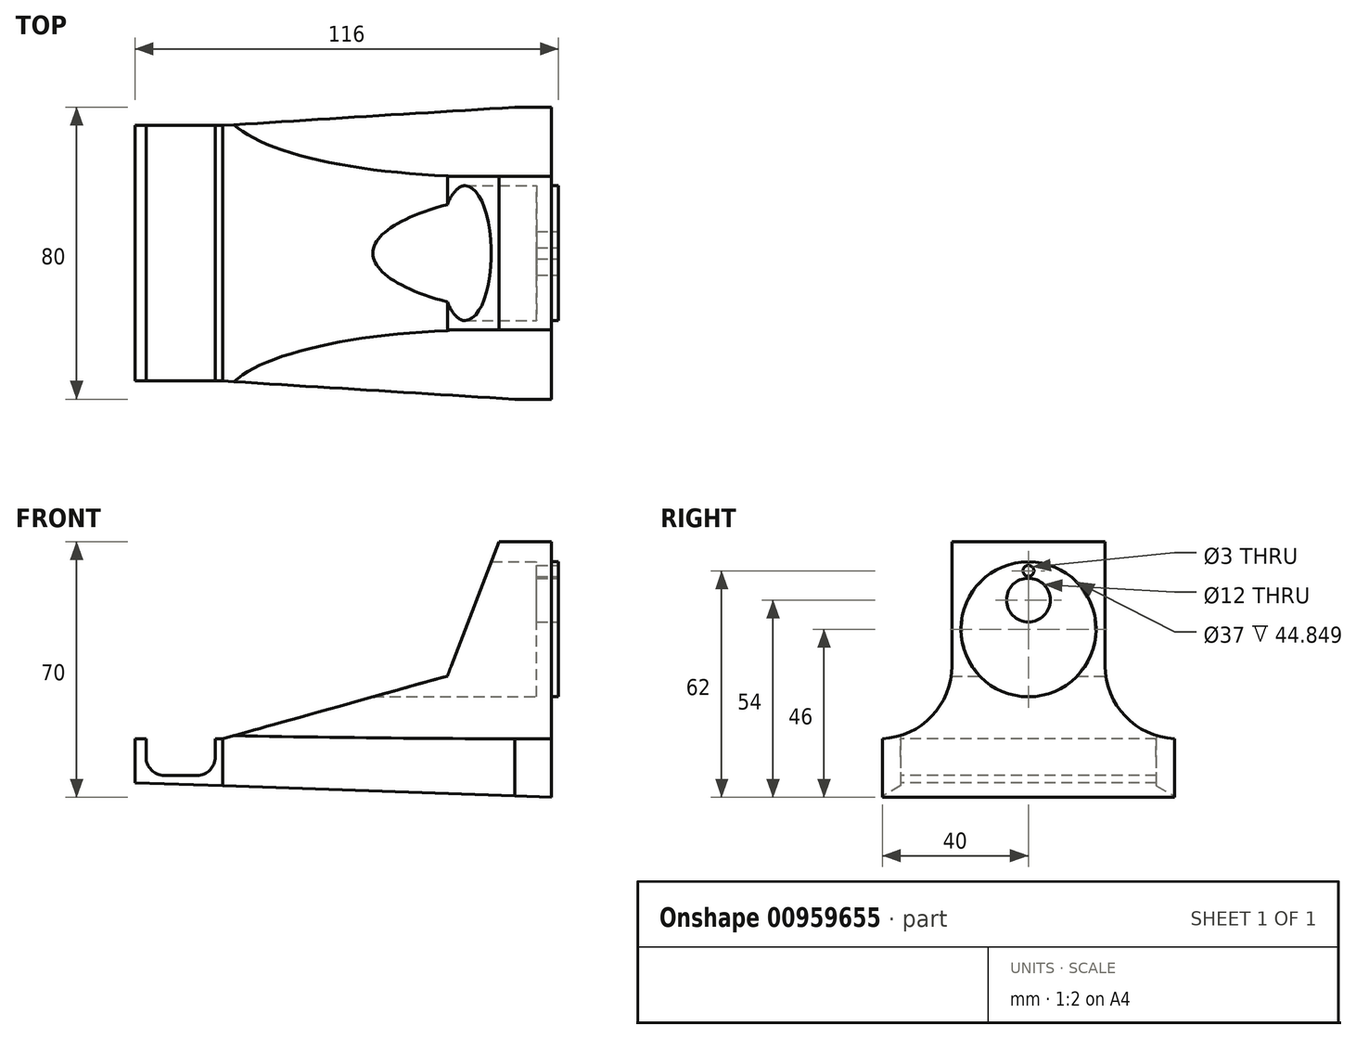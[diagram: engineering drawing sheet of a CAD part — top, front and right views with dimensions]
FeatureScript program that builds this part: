
annotation { "Feature Type Name" : "Feature", "Feature Type Description" : "" }
export const myFeature = defineFeature(function(context is Context, id is Id, definition is map)
    precondition{}
    {
        {
            var Q0;
            Q0=qCreatedBy(makeId("Right.planeOp"),FACE);
            var sketch = newSketch(context, id + "F0", { "sketchPlane" : qUnion([Q0])});
            skCircle(sketch, "E0", {"center": v(0, 0) * mm, "radius": 18.5 * mm});
            skSolve(sketch);
        }
        {
            var Q0;
            Q0=makeQuery(id+"F0.imprint","IMPRINT",FACE,{"disambiguationData":[TD([[makeQuery(id+"F0.imprint","IMPRINT",EDGE,{"derivedFrom":sQuery(id+"F0.wireOp",EDGE,"E0")}),1.0]])]});
            extrude(context, id + "F1", {"entities" : qUnion([Q0]), "depth" : 2 * mm, "offsetDistance" : 25 * mm});
        }
        {
            var Q0;
            Q0=makeQuery(id+"F1.opExtrude","CAP_FACE",FACE,{"disambiguationData":[OSD([sQuery(id+"F0.wireOp",EDGE,"E0")])],"isStart":false});
            var sketch = newSketch(context, id + "F2", { "sketchPlane" : qUnion([Q0])});
            skCircle(sketch, "E1", {"center": v(0, 16) * mm, "radius": 1.5 * mm});
            skSolve(sketch);
        }
        {
            var Q0;
            Q0=makeQuery(id+"F2.imprint","IMPRINT",FACE,{"disambiguationData":[TD([[makeQuery(id+"F2.imprint","IMPRINT",EDGE,{"derivedFrom":sQuery(id+"F2.wireOp",EDGE,"E1")}),1.0]])]});
            extrude(context, id + "F3", {"entities" : qUnion([Q0]), "operationType" : NewBodyOperationType.REMOVE, "oppositeDirection" : true, "depth" : 25 * mm, "offsetDistance" : 25 * mm});
        }
        {
            var Q0;
            Q0=qCreatedBy(makeId("Top.planeOp"),FACE);
            var sketch = newSketch(context, id + "F4", { "sketchPlane" : qUnion([Q0])});
            skLineSegment(sketch, "E2", {"start": v(0, 0) * mm, "end": v(32.12, 0) * mm, "construction": true});
            skSolve(sketch);
        }
        {
            var Q0;
            Q0=makeQuery(id+"F1.opExtrude","CAP_FACE",FACE,{"disambiguationData":[OSD([sQuery(id+"F0.wireOp",EDGE,"E0")])],"isStart":false});
            var sketch = newSketch(context, id + "F5", { "sketchPlane" : qUnion([Q0])});
            skCircle(sketch, "E3", {"center": v(0, 8) * mm, "radius": 6 * mm});
            skSolve(sketch);
        }
        {
            var Q0;
            Q0=makeQuery(id+"F5.imprint","IMPRINT",FACE,{"disambiguationData":[TD([[makeQuery(id+"F5.imprint","IMPRINT",EDGE,{"derivedFrom":sQuery(id+"F5.wireOp",EDGE,"E3")}),1.0]])]});
            extrude(context, id + "F6", {"entities" : qUnion([Q0]), "operationType" : NewBodyOperationType.REMOVE, "oppositeDirection" : true, "depth" : 25 * mm, "offsetDistance" : 25 * mm});
        }
        {
            var Q0;
            Q0=qCreatedBy(makeId("Right.planeOp"),FACE);
            var sketch = newSketch(context, id + "F7", { "sketchPlane" : qUnion([Q0])});
            skLineSegment(sketch, "E4.bottom", {"start": v(-21, -46) * mm, "end": v(21, -46) * mm});
            skLineSegment(sketch, "E4.top", {"start": v(-21, 24) * mm, "end": v(21, 24) * mm});
            skLineSegment(sketch, "E4.left", {"start": v(-21, -46) * mm, "end": v(-21, 24) * mm});
            skLineSegment(sketch, "E4.right", {"start": v(21, -46) * mm, "end": v(21, 24) * mm});
            skPoint(sketch, "E4.middle", {"position": v(0, -11) * mm});
            skLineSegment(sketch, "E5.bottom", {"start": v(-40, -46) * mm, "end": v(40, -46) * mm});
            skLineSegment(sketch, "E5.top", {"start": v(-40, -30) * mm, "end": v(40, -30) * mm});
            skLineSegment(sketch, "E5.left", {"start": v(-40, -46) * mm, "end": v(-40, -30) * mm});
            skLineSegment(sketch, "E5.right", {"start": v(40, -46) * mm, "end": v(40, -30) * mm});
            skPoint(sketch, "E5.middle", {"position": v(0, -38) * mm});
            skPoint(sketch, "E5.cornerSnap0", {"position": v(0, -46) * mm});
            skSolve(sketch);
        }
        {
            var Q0;
            {var subQ0=sQuery(id+"F7.wireOp",EDGE,"E4.top");Q0=makeQuery(id+"F7.imprint","IMPRINT",FACE,{"disambiguationData":[TD([[makeQuery(id+"F7.imprint","IMPRINT",EDGE,{"derivedFrom":subQ0}),-1.0]])]});}
            var Q1;
            {var subQ5=sQuery(id+"F7.wireOp",EDGE,"E5.right");Q1=makeQuery(id+"F7.imprint","IMPRINT",FACE,{"disambiguationData":[TD([[makeQuery(id+"F7.imprint","IMPRINT",EDGE,{"derivedFrom":subQ5}),1.0]])]});}
            var Q2;
            {var subQ0=sQuery(id+"F7.wireOp",EDGE,"E5.bottom");var subQ1=sQuery(id+"F7.wireOp",EDGE,"E4.left");var subQ2=makeQuery(id+"F7.imprint","INTERSECT",VERTEX,{"derivedFrom":[subQ1,subQ0]});Q2=makeQuery(id+"F7.imprint","IMPRINT",FACE,{"disambiguationData":[TD([[makeQuery(id+"F7.imprint","IMPRINT",EDGE,{"disambiguationData":[TD([[subQ2,-1.0]])],"derivedFrom":subQ1}),-1.0]])]});}
            var Q3;
            {var subQ5=sQuery(id+"F7.wireOp",EDGE,"E5.left");Q3=makeQuery(id+"F7.imprint","IMPRINT",FACE,{"disambiguationData":[TD([[makeQuery(id+"F7.imprint","IMPRINT",EDGE,{"derivedFrom":subQ5}),-1.0]])]});}
            extrude(context, id + "F8", {"entities" : qUnion([Q0, Q1, Q2, Q3]), "operationType" : NewBodyOperationType.ADD, "oppositeDirection" : true, "depth" : 90 * mm, "offsetDistance" : 25 * mm});
        }
        {
            var Q0;
            Q0=qCreatedBy(makeId("Right.planeOp"),FACE);
            cPlane(context, id + "F9", {"entities" : qUnion([Q0]), "cplaneType" : CPlaneType.OFFSET, "offset" : 4 * mm, "oppositeDirection" : true, "width" : 150 * mm, "height" : 150 * mm});
        }
        {
            var Q0;
            Q0=qCreatedBy(id+"F9.planeOp",FACE);
            var sketch = newSketch(context, id + "F10", { "sketchPlane" : qUnion([Q0])});
            skCircle(sketch, "E6", {"center": v(0, 0) * mm, "radius": 18.5 * mm});
            skSolve(sketch);
        }
        {
            var Q0;
            Q0 = qSketchRegion(id + "F10", true);
            var Q1;
            Q1=makeQuery(id+"F8.boolean.opBoolean","SPLIT",FACE,{"disambiguationData":[TD([makeQuery(id+"F6.boolean.opBoolean","COPY",FACE,{"derivedFrom":makeQuery(id+"F6.opExtrude","SWEPT_FACE",FACE,{"disambiguationData":[OSD([sQuery(id+"F5.wireOp",EDGE,"E3")])]})})])],"derivedFrom":makeQuery(id+"F8.opExtrude","CAP_FACE",FACE,{"disambiguationData":[OSD([sQuery(id+"F7.wireOp",EDGE,"E4.top"),sQuery(id+"F7.wireOp",EDGE,"E4.left"),sQuery(id+"F7.wireOp",EDGE,"E4.right"),sQuery(id+"F7.wireOp",EDGE,"E5.bottom"),sQuery(id+"F7.wireOp",EDGE,"E5.top"),sQuery(id+"F7.wireOp",EDGE,"E5.left"),sQuery(id+"F7.wireOp",EDGE,"E5.right")])],"isStart":true})});
            extrude(context, id + "F11", {"entities" : qUnion([Q0, Q1]), "operationType" : NewBodyOperationType.REMOVE, "oppositeDirection" : true, "depth" : 80 * mm, "offsetDistance" : 25 * mm});
        }
        {
            var Q0;
            Q0=makeQuery(id+"F8.opExtrude","SWEPT_FACE",FACE,{"disambiguationData":[OSD([sQuery(id+"F7.wireOp",EDGE,"E4.right")])]});
            var sketch = newSketch(context, id + "F12", { "sketchPlane" : qUnion([Q0])});
            skLineSegment(sketch, "E7", {"start": v(14.3, 24) * mm, "end": v(28.45, -12.8) * mm});
            skLineSegment(sketch, "E8", {"start": v(28.45, -12.8) * mm, "end": v(90, -30) * mm});
            skLineSegment(sketch, "E9", {"start": v(90, -30) * mm, "end": v(90, 24) * mm});
            skLineSegment(sketch, "E10", {"start": v(90, 24) * mm, "end": v(14.3, 24) * mm});
            skSolve(sketch);
        }
        {
            var Q0;
            Q0=makeQuery(id+"F12.imprint","IMPRINT",FACE,{"disambiguationData":[TD([[makeQuery(id+"F12.imprint","IMPRINT",EDGE,{"derivedFrom":sQuery(id+"F12.wireOp",EDGE,"E7")}),1.0]])]});
            extrude(context, id + "F13", {"entities" : qUnion([Q0]), "operationType" : NewBodyOperationType.REMOVE, "endBound" : BoundingType.THROUGH_ALL, "oppositeDirection" : true, "depth" : 25 * mm, "offsetDistance" : 25 * mm});
        }
        {
            var Q0;
            Q0=makeQuery(id+"F8.boolean.opBoolean","SPLIT",FACE,{"disambiguationData":[TD([makeQuery(id+"F5O549hGg848MVX_1.1.F6.boolean.opBoolean","COPY",FACE,{"derivedFrom":makeQuery(id+"F5O549hGg848MVX_1.1.F6.opExtrude","SWEPT_FACE",FACE,{"disambiguationData":[OSD([sQuery(id+"F5.wireOp",EDGE,"E3")])]})})])],"derivedFrom":makeQuery(id+"F8.opExtrude","CAP_FACE",FACE,{"disambiguationData":[OSD([sQuery(id+"F7.wireOp",EDGE,"E4.top"),sQuery(id+"F7.wireOp",EDGE,"E4.left"),sQuery(id+"F7.wireOp",EDGE,"E4.right"),sQuery(id+"F7.wireOp",EDGE,"E5.bottom"),sQuery(id+"F7.wireOp",EDGE,"E5.top"),sQuery(id+"F7.wireOp",EDGE,"E5.left"),sQuery(id+"F7.wireOp",EDGE,"E5.right")])],"isStart":true})});
            var Q1;
            Q1=makeQuery(id+"F8.boolean.opBoolean","SPLIT",FACE,{"disambiguationData":[TD([makeQuery(id+"F3.boolean.opBoolean","COPY",FACE,{"derivedFrom":makeQuery(id+"F3.opExtrude","SWEPT_FACE",FACE,{"disambiguationData":[OSD([sQuery(id+"F2.wireOp",EDGE,"E1")])]})})])],"derivedFrom":makeQuery(id+"F8.opExtrude","CAP_FACE",FACE,{"disambiguationData":[OSD([sQuery(id+"F7.wireOp",EDGE,"E4.top"),sQuery(id+"F7.wireOp",EDGE,"E4.left"),sQuery(id+"F7.wireOp",EDGE,"E4.right"),sQuery(id+"F7.wireOp",EDGE,"E5.bottom"),sQuery(id+"F7.wireOp",EDGE,"E5.top"),sQuery(id+"F7.wireOp",EDGE,"E5.left"),sQuery(id+"F7.wireOp",EDGE,"E5.right")])],"isStart":true})});
            var Q2;
            Q2=makeQuery(id+"F8.boolean.opBoolean","SPLIT",FACE,{"disambiguationData":[TD([makeQuery(id+"F37mEyM0ohrxXI6_1.1.F3.boolean.opBoolean","COPY",FACE,{"derivedFrom":makeQuery(id+"F37mEyM0ohrxXI6_1.1.F3.opExtrude","SWEPT_FACE",FACE,{"disambiguationData":[OSD([sQuery(id+"F2.wireOp",EDGE,"E1")])]})})])],"derivedFrom":makeQuery(id+"F8.opExtrude","CAP_FACE",FACE,{"disambiguationData":[OSD([sQuery(id+"F7.wireOp",EDGE,"E4.top"),sQuery(id+"F7.wireOp",EDGE,"E4.left"),sQuery(id+"F7.wireOp",EDGE,"E4.right"),sQuery(id+"F7.wireOp",EDGE,"E5.bottom"),sQuery(id+"F7.wireOp",EDGE,"E5.top"),sQuery(id+"F7.wireOp",EDGE,"E5.left"),sQuery(id+"F7.wireOp",EDGE,"E5.right")])],"isStart":true})});
            var Q3;
            Q3=makeQuery(id+"F8.boolean.opBoolean","SPLIT",FACE,{"disambiguationData":[TD([makeQuery(id+"F37mEyM0ohrxXI6_1.2.F3.boolean.opBoolean","COPY",FACE,{"derivedFrom":makeQuery(id+"F37mEyM0ohrxXI6_1.2.F3.opExtrude","SWEPT_FACE",FACE,{"disambiguationData":[OSD([sQuery(id+"F2.wireOp",EDGE,"E1")])]})})])],"derivedFrom":makeQuery(id+"F8.opExtrude","CAP_FACE",FACE,{"disambiguationData":[OSD([sQuery(id+"F7.wireOp",EDGE,"E4.top"),sQuery(id+"F7.wireOp",EDGE,"E4.left"),sQuery(id+"F7.wireOp",EDGE,"E4.right"),sQuery(id+"F7.wireOp",EDGE,"E5.bottom"),sQuery(id+"F7.wireOp",EDGE,"E5.top"),sQuery(id+"F7.wireOp",EDGE,"E5.left"),sQuery(id+"F7.wireOp",EDGE,"E5.right")])],"isStart":true})});
            extrude(context, id + "F14", {"entities" : qUnion([Q0, Q1, Q2, Q3]), "operationType" : NewBodyOperationType.REMOVE, "oppositeDirection" : true, "depth" : 25 * mm, "offsetDistance" : 25 * mm});
        }
        {
            var Q0;
            Q0=makeQuery(id+"F8.opExtrude","CAP_FACE",FACE,{"disambiguationData":[OSD([sQuery(id+"F7.wireOp",EDGE,"E4.top"),sQuery(id+"F7.wireOp",EDGE,"E4.left"),sQuery(id+"F7.wireOp",EDGE,"E4.right"),sQuery(id+"F7.wireOp",EDGE,"E5.bottom"),sQuery(id+"F7.wireOp",EDGE,"E5.top"),sQuery(id+"F7.wireOp",EDGE,"E5.left"),sQuery(id+"F7.wireOp",EDGE,"E5.right")])],"isStart":false});
            var sketch = newSketch(context, id + "F15", { "sketchPlane" : qUnion([Q0])});
            skLineSegment(sketch, "E11.bottom", {"start": v(-35, -30) * mm, "end": v(35, -30) * mm});
            skLineSegment(sketch, "E11.top", {"start": v(-35, -46) * mm, "end": v(35, -46) * mm});
            skLineSegment(sketch, "E11.left", {"start": v(-35, -30) * mm, "end": v(-35, -46) * mm});
            skLineSegment(sketch, "E11.right", {"start": v(35, -30) * mm, "end": v(35, -46) * mm});
            skSolve(sketch);
        }
        {
            var Q0;
            Q0=makeQuery(id+"F15.imprint","IMPRINT",FACE,{"disambiguationData":[TD([[makeQuery(id+"F15.imprint","IMPRINT",EDGE,{"derivedFrom":sQuery(id+"F15.wireOp",EDGE,"E11.top")}),-1.0]])]});
            extrude(context, id + "F16", {"entities" : qUnion([Q0]), "operationType" : NewBodyOperationType.ADD, "depth" : 24 * mm, "offsetDistance" : 25 * mm});
        }
        {
            var Q0;
            Q0=makeQuery(id+"F16.opExtrude","SWEPT_FACE",FACE,{"disambiguationData":[OSD([sQuery(id+"F15.wireOp",EDGE,"E11.right")])]});
            var sketch = newSketch(context, id + "F17", { "sketchPlane" : qUnion([Q0])});
            skLineSegment(sketch, "E12", {"start": v(-114, -42) * mm, "end": v(0, -46) * mm});
            skLineSegment(sketch, "E13", {"start": v(0, -46) * mm, "end": v(-114, -46) * mm});
            skLineSegment(sketch, "E14", {"start": v(-114, -46) * mm, "end": v(-114, -42) * mm});
            skSolve(sketch);
        }
        {
            var Q0;
            Q0 = qSketchRegion(id + "F17", true);
            extrude(context, id + "F18", {"entities" : qUnion([Q0]), "operationType" : NewBodyOperationType.REMOVE, "endBound" : BoundingType.THROUGH_ALL, "oppositeDirection" : true, "depth" : 25 * mm, "offsetDistance" : 25 * mm, "hasSecondDirection" : true, "secondDirectionOppositeDirection" : false, "secondDirectionDepth" : 25 * mm});
        }
        {
            var Q0;
            {var subQ0=sQuery(id+"F7.wireOp",EDGE,"E5.top");Q0=makeQuery(id+"F16.boolean.opBoolean","MERGE",FACE,{"derivedFrom":[makeQuery(id+"F8.opExtrude","SWEPT_FACE",FACE,{"disambiguationData":[OSD([subQ0]),TDD([makeQuery(id+"F7.imprint","IMPRINT",EDGE,{"disambiguationData":[TD([[makeQuery(id+"F7.imprint","INTERSECT",VERTEX,{"derivedFrom":[subQ0,sQuery(id+"F7.wireOp",EDGE,"E5.left")]}),-1.0]])],"derivedFrom":subQ0})])]}),makeQuery(id+"F8.opExtrude","SWEPT_FACE",FACE,{"disambiguationData":[OSD([subQ0]),TDD([makeQuery(id+"F7.imprint","IMPRINT",EDGE,{"disambiguationData":[TD([[makeQuery(id+"F7.imprint","INTERSECT",VERTEX,{"derivedFrom":[subQ0,sQuery(id+"F7.wireOp",EDGE,"E5.right")]}),1.0]])],"derivedFrom":subQ0})])]}),makeQuery(id+"F16.opExtrude","SWEPT_FACE",FACE,{"disambiguationData":[OSD([sQuery(id+"F15.wireOp",EDGE,"E11.bottom")])]})]});}
            var sketch = newSketch(context, id + "F19", { "sketchPlane" : qUnion([Q0])});
            skLineSegment(sketch, "E15.bottom", {"start": v(-111, 35) * mm, "end": v(-92, 35) * mm});
            skLineSegment(sketch, "E15.top", {"start": v(-111, -35) * mm, "end": v(-92, -35) * mm});
            skLineSegment(sketch, "E15.left", {"start": v(-111, 35) * mm, "end": v(-111, -35) * mm});
            skLineSegment(sketch, "E15.right", {"start": v(-92, 35) * mm, "end": v(-92, -35) * mm});
            skSolve(sketch);
        }
        {
            var Q0;
            Q0=makeQuery(id+"F19.imprint","IMPRINT",FACE,{"disambiguationData":[TD([[makeQuery(id+"F19.imprint","IMPRINT",EDGE,{"derivedFrom":sQuery(id+"F19.wireOp",EDGE,"E15.bottom")}),-1.0]])]});
            extrude(context, id + "F20", {"entities" : qUnion([Q0]), "operationType" : NewBodyOperationType.REMOVE, "oppositeDirection" : true, "depth" : 10 * mm, "offsetDistance" : 25 * mm});
        }
        {
            var Q0;
            Q0=makeQuery(id+"F8.opExtrude","SWEPT_EDGE",EDGE,{"disambiguationData":[OSD([sQuery(id+"F7.wireOp",EDGE,"E4.left"),sQuery(id+"F7.wireOp",EDGE,"E5.top")])]});
            var Q1;
            Q1=makeQuery(id+"F8.opExtrude","SWEPT_EDGE",EDGE,{"disambiguationData":[OSD([sQuery(id+"F7.wireOp",EDGE,"E4.right"),sQuery(id+"F7.wireOp",EDGE,"E5.top")])]});
            fillet(context, id + "F21", {"entities" : qUnion([Q0, Q1]), "radius" : 20 * mm, "tangentPropagation" : true, "allowEdgeOverflow" : false});
        }
        {
            var Q0;
            Q0=makeQuery(id+"F8.opExtrude","CAP_EDGE",EDGE,{"disambiguationData":[OSD([sQuery(id+"F7.wireOp",EDGE,"E5.left")])],"isStart":false});
            chamfer(context, id + "F22", {"entities" : qUnion([Q0]), "chamferType" : ChamferType.TWO_OFFSETS, "width1" : 5 * mm, "oppositeDirection" : false, "width2" : 80 * mm, "tangentPropagation" : true});
        }
        {
            var Q0;
            Q0=makeQuery(id+"F8.opExtrude","CAP_EDGE",EDGE,{"disambiguationData":[OSD([sQuery(id+"F7.wireOp",EDGE,"E5.right")])],"isStart":false});
            chamfer(context, id + "F23", {"entities" : qUnion([Q0]), "chamferType" : ChamferType.TWO_OFFSETS, "width1" : 80 * mm, "oppositeDirection" : false, "width2" : 5 * mm, "tangentPropagation" : true});
        }
        {
            var Q0;
            Q0=makeQuery(id+"F20.boolean.opBoolean","COPY",EDGE,{"derivedFrom":makeQuery(id+"F20.opExtrude","CAP_EDGE",EDGE,{"disambiguationData":[OSD([sQuery(id+"F19.wireOp",EDGE,"E15.left")])],"isStart":false})});
            var Q1;
            Q1=makeQuery(id+"F20.boolean.opBoolean","COPY",EDGE,{"derivedFrom":makeQuery(id+"F20.opExtrude","CAP_EDGE",EDGE,{"disambiguationData":[OSD([sQuery(id+"F19.wireOp",EDGE,"E15.right")])],"isStart":false})});
            fillet(context, id + "F24", {"entities" : qUnion([Q0, Q1]), "radius" : 5 * mm, "tangentPropagation" : true, "allowEdgeOverflow" : false});
        }
    });
